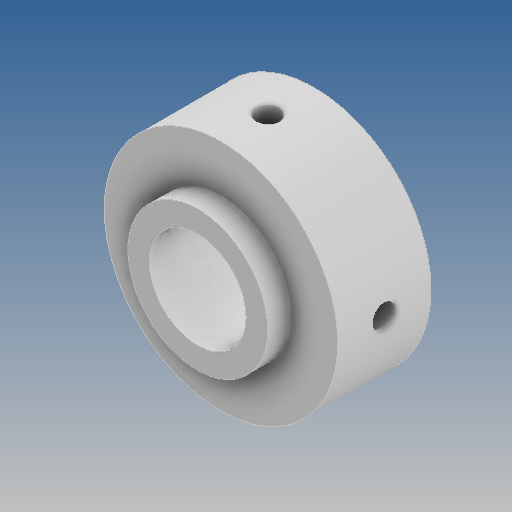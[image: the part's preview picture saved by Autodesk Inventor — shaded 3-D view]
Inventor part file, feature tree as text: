
AUTODESK INVENTOR PART (.ipt)
format: ipt  version: 2020 (Build 240168000, 168)  size: 163,840 bytes
history: native  units: mm
features: sketch x4, extrude x2, hole x2
ambient origin geometry x8: Origin, YZ Plane, XZ Plane, XY Plane, X Axis, Y Axis, Z Axis, Center Point
bodies: Solid1 (feature_tree)
feature tree (8):
  extrude  "Extrusion1"  Depth=20.0mm
  hole  "Hole1"  [1 undecoded]
  hole  "Hole2"  [1 undecoded]
  extrude  "Extrusion2"  Depth=4.0mm
  sketch  "Sketch1"  dims[d0=8.3mm d1=20.0mm]
  sketch  "Sketch2"  dims[d2=10.0mm d3=0.0mm]
  sketch  "Sketch3"  dims[d4=2.0mm d5=6.0mm d6=8.0mm d7=6.0mm d8=90.0deg d9=8.0mm d10=20.594885mm d11=4.0mm]
  sketch  "Sketch4"  dims[d12=2.0mm d13=6.0mm d14=8.0mm d15=6.0mm d16=90.0deg d17=8.0mm d18=20.594885mm d19=2.0mm d20=0.0mm d21=12.0mm d22=4.0mm]
note: 2 required parameter values undecoded (feature->parameter linkage not recoverable at this tier; creation-order binding heuristic only, values carry confidence <= 0.55)
